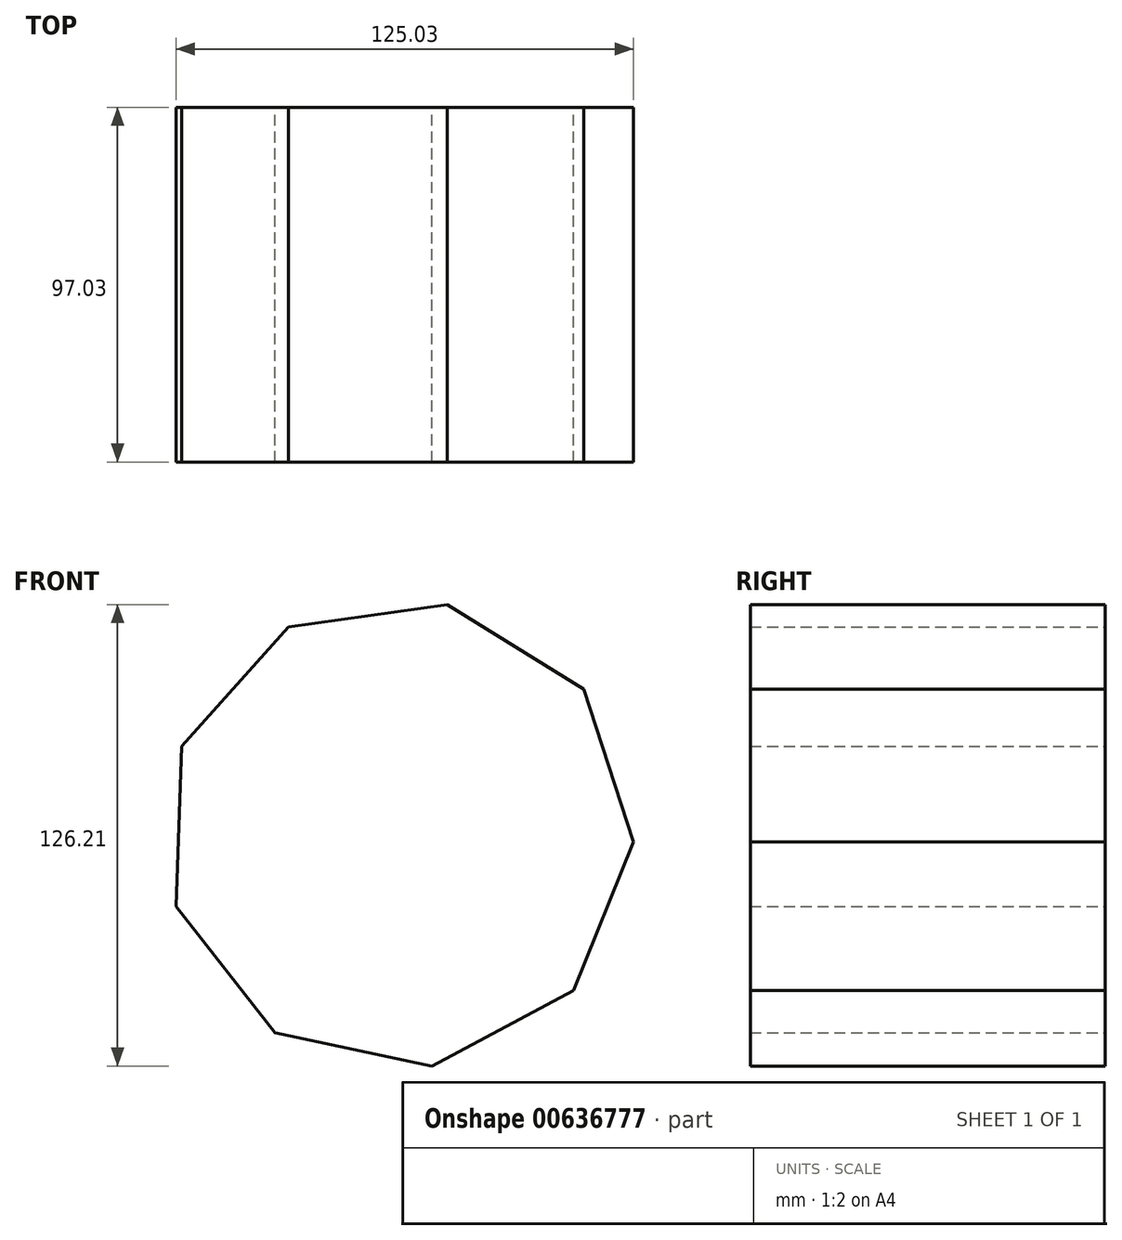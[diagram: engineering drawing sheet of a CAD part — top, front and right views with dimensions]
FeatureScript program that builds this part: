
annotation { "Feature Type Name" : "Feature", "Feature Type Description" : "" }
export const myFeature = defineFeature(function(context is Context, id is Id, definition is map)
    precondition{}
    {
        {
            var Q0;
            Q0=qCreatedBy(makeId("Front.planeOp"),FACE);
            var sketch = newSketch(context, id + "F0", { "sketchPlane" : qUnion([Q0])});
            skCircle(sketch, "E0.cCircle", {"center": v(0, 0) * mm, "radius": 60.25 * mm, "construction": true});
            skLineSegment(sketch, "E0.0", {"start": v(13.25, 62.73) * mm, "end": v(50.47, 39.54) * mm});
            skLineSegment(sketch, "E0.1", {"start": v(50.47, 39.54) * mm, "end": v(64.08, -2.15) * mm});
            skLineSegment(sketch, "E0.2", {"start": v(64.08, -2.15) * mm, "end": v(47.7, -42.84) * mm});
            skLineSegment(sketch, "E0.3", {"start": v(47.7, -42.84) * mm, "end": v(9, -63.48) * mm});
            skLineSegment(sketch, "E0.4", {"start": v(9, -63.48) * mm, "end": v(-33.9, -54.42) * mm});
            skLineSegment(sketch, "E0.5", {"start": v(-33.9, -54.42) * mm, "end": v(-60.95, -19.9) * mm});
            skLineSegment(sketch, "E0.6", {"start": v(-60.95, -19.9) * mm, "end": v(-59.48, 23.94) * mm});
            skLineSegment(sketch, "E0.7", {"start": v(-59.48, 23.94) * mm, "end": v(-30.18, 56.57) * mm});
            skLineSegment(sketch, "E0.8", {"start": v(-30.18, 56.57) * mm, "end": v(13.25, 62.73) * mm});
            skPoint(sketch, "E0.0.midPoint", {"position": v(31.86, 51.14) * mm});
            skSolve(sketch);
        }
        {
            var Q0;
            Q0=makeQuery(id+"F0.imprint","IMPRINT",FACE,{"disambiguationData":[TD([[makeQuery(id+"F0.imprint","IMPRINT",EDGE,{"derivedFrom":sQuery(id+"F0.wireOp",EDGE,"E0.0")}),-1.0]])]});
            extrude(context, id + "F1", {"entities" : qUnion([Q0]), "depth" : 97.03 * mm, "offsetDistance" : 25.4 * mm});
        }
    });
